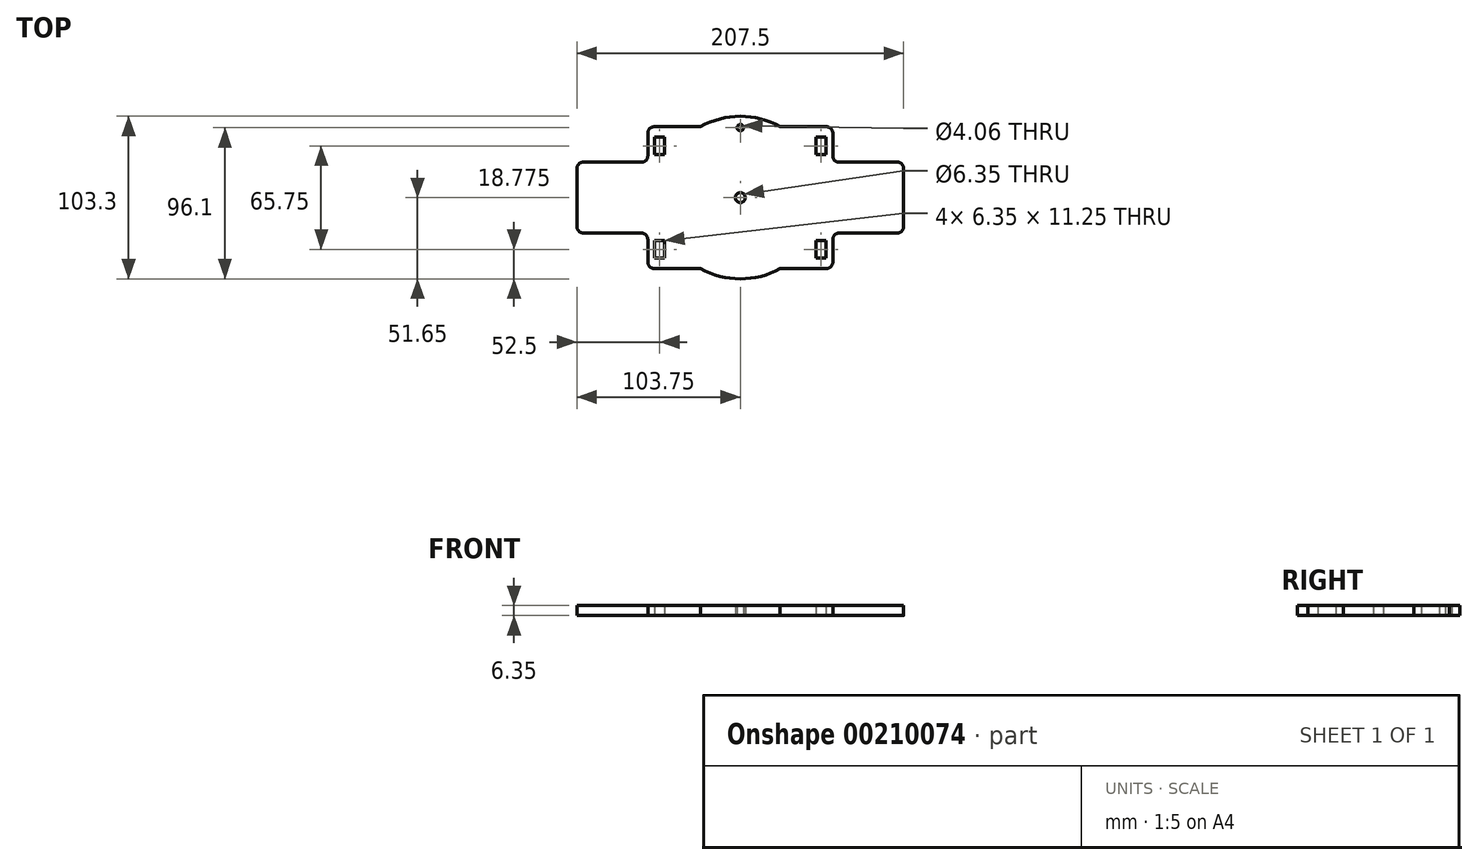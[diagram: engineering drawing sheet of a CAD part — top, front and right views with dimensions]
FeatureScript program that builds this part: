
annotation { "Feature Type Name" : "Feature", "Feature Type Description" : "" }
export const myFeature = defineFeature(function(context is Context, id is Id, definition is map)
    precondition{}
    {
        {
            var Q0;
            Q0=qCreatedBy(makeId("Top.planeOp"),FACE);
            var sketch = newSketch(context, id + "F0", { "sketchPlane" : qUnion([Q0])});
            skCircle(sketch, "E0", {"center": v(0, 0) * mm, "radius": 51.65 * mm});
            skLineSegment(sketch, "E1.bottom", {"start": v(-54.75, 45) * mm, "end": v(103.75, 45) * mm});
            skLineSegment(sketch, "E1.top", {"start": v(-103.75, -45) * mm, "end": v(103.75, -45) * mm});
            skLineSegment(sketch, "E1.left", {"start": v(-103.75, 18.5) * mm, "end": v(-103.75, -45) * mm});
            skLineSegment(sketch, "E1.right", {"start": v(103.75, 45) * mm, "end": v(103.75, -45) * mm});
            skLineSegment(sketch, "E2", {"start": v(-103.75, 0) * mm, "end": v(103.75, 0) * mm, "construction": true});
            skLineSegment(sketch, "E3", {"start": v(0, 51.65) * mm, "end": v(0, -51.65) * mm, "construction": true});
            skPoint(sketch, "E3.endSnap0", {"position": v(0, -45) * mm});
            skLineSegment(sketch, "E4.bottom", {"start": v(-54.43, 38.5) * mm, "end": v(-48.08, 38.5) * mm});
            skLineSegment(sketch, "E4.top", {"start": v(-54.43, 27.25) * mm, "end": v(-48.08, 27.25) * mm});
            skLineSegment(sketch, "E4.left", {"start": v(-54.43, 38.5) * mm, "end": v(-54.43, 27.25) * mm});
            skLineSegment(sketch, "E4.right", {"start": v(-48.08, 38.5) * mm, "end": v(-48.08, 27.25) * mm});
            skPoint(sketch, "E4.middle", {"position": v(-51.25, 32.88) * mm});
            skLineSegment(sketch, "E5.bottom", {"start": v(-54.43, -27.25) * mm, "end": v(-48.08, -27.25) * mm});
            skLineSegment(sketch, "E5.top", {"start": v(-54.43, -38.5) * mm, "end": v(-48.08, -38.5) * mm});
            skLineSegment(sketch, "E5.left", {"start": v(-54.43, -27.25) * mm, "end": v(-54.43, -38.5) * mm});
            skLineSegment(sketch, "E5.right", {"start": v(-48.08, -27.25) * mm, "end": v(-48.08, -38.5) * mm});
            skPoint(sketch, "E5.middle", {"position": v(-51.25, -32.88) * mm});
            skLineSegment(sketch, "E6.bottom", {"start": v(54.43, -27.25) * mm, "end": v(48.08, -27.25) * mm});
            skLineSegment(sketch, "E6.top", {"start": v(54.43, -38.5) * mm, "end": v(48.08, -38.5) * mm});
            skLineSegment(sketch, "E6.left", {"start": v(54.43, -27.25) * mm, "end": v(54.43, -38.5) * mm});
            skLineSegment(sketch, "E6.right", {"start": v(48.08, -27.25) * mm, "end": v(48.08, -38.5) * mm});
            skPoint(sketch, "E6.middle", {"position": v(51.25, -32.87) * mm});
            skLineSegment(sketch, "E7.bottom", {"start": v(48.08, 38.5) * mm, "end": v(54.43, 38.5) * mm});
            skLineSegment(sketch, "E7.top", {"start": v(48.08, 27.25) * mm, "end": v(54.43, 27.25) * mm});
            skLineSegment(sketch, "E7.left", {"start": v(48.08, 38.5) * mm, "end": v(48.08, 27.25) * mm});
            skLineSegment(sketch, "E7.right", {"start": v(54.43, 38.5) * mm, "end": v(54.43, 27.25) * mm});
            skPoint(sketch, "E7.middle", {"position": v(51.25, 32.88) * mm});
            skLineSegment(sketch, "E8", {"start": v(-99.75, 22.5) * mm, "end": v(-62.75, 22.5) * mm});
            skLineSegment(sketch, "E9", {"start": v(-58.75, 26.5) * mm, "end": v(-58.75, 41) * mm});
            skPoint(sketch, "E10.newPointA", {"position": v(-103.75, 22.5) * mm});
            skPoint(sketch, "E10.newPointB", {"position": v(-103.75, 45) * mm});
            skArc(sketch, "E10.filletArc", {"start": v(-99.75, 22.5) * mm, "mid": v(-102.58, 21.33) * mm, "end": v(-103.75, 18.5) * mm});
            skPoint(sketch, "E11.visualSharp", {"position": v(-58.75, 22.5) * mm});
            skArc(sketch, "E11.filletArc", {"start": v(-62.75, 22.5) * mm, "mid": v(-59.92, 23.67) * mm, "end": v(-58.75, 26.5) * mm});
            skPoint(sketch, "E12.newPointA", {"position": v(-58.75, 45) * mm});
            skArc(sketch, "E12.filletArc", {"start": v(-54.75, 45) * mm, "mid": v(-57.58, 43.83) * mm, "end": v(-58.75, 41) * mm});
            skArc(sketch, "E13.MirrorCS", {"start": v(-54.75, -45) * mm, "mid": v(-57.58, -43.83) * mm, "end": v(-58.75, -41) * mm});
            skLineSegment(sketch, "E14.MirrorCS", {"start": v(-99.75, -22.5) * mm, "end": v(-62.75, -22.5) * mm});
            skLineSegment(sketch, "E15.MirrorCS", {"start": v(-58.75, -26.5) * mm, "end": v(-58.75, -41) * mm});
            skArc(sketch, "E16.MirrorCS", {"start": v(-62.75, -22.5) * mm, "mid": v(-59.92, -23.67) * mm, "end": v(-58.75, -26.5) * mm});
            skArc(sketch, "E17.MirrorCS", {"start": v(-99.75, -22.5) * mm, "mid": v(-102.58, -21.33) * mm, "end": v(-103.75, -18.5) * mm});
            skArc(sketch, "E18.MirrorCS", {"start": v(54.75, -45) * mm, "mid": v(57.58, -43.83) * mm, "end": v(58.75, -41) * mm});
            skLineSegment(sketch, "E19.MirrorCS", {"start": v(58.75, -26.5) * mm, "end": v(58.75, -41) * mm});
            skArc(sketch, "E20.MirrorCS", {"start": v(62.75, -22.5) * mm, "mid": v(59.92, -23.67) * mm, "end": v(58.75, -26.5) * mm});
            skLineSegment(sketch, "E21.MirrorCS", {"start": v(99.75, -22.5) * mm, "end": v(62.75, -22.5) * mm});
            skArc(sketch, "E22.MirrorCS", {"start": v(99.75, -22.5) * mm, "mid": v(102.58, -21.33) * mm, "end": v(103.75, -18.5) * mm});
            skArc(sketch, "E23.MirrorCS", {"start": v(54.75, 45) * mm, "mid": v(57.58, 43.83) * mm, "end": v(58.75, 41) * mm});
            skLineSegment(sketch, "E24.MirrorCS", {"start": v(99.75, 22.5) * mm, "end": v(62.75, 22.5) * mm});
            skLineSegment(sketch, "E25.MirrorCS", {"start": v(58.75, 26.5) * mm, "end": v(58.75, 41) * mm});
            skArc(sketch, "E26.MirrorCS", {"start": v(62.75, 22.5) * mm, "mid": v(59.92, 23.67) * mm, "end": v(58.75, 26.5) * mm});
            skArc(sketch, "E27.MirrorCS", {"start": v(99.75, 22.5) * mm, "mid": v(102.58, 21.33) * mm, "end": v(103.75, 18.5) * mm});
            skCircle(sketch, "E28", {"center": v(0, 0) * mm, "radius": 3.17 * mm});
            skCircle(sketch, "E29", {"center": v(0, 44.45) * mm, "radius": 2.03 * mm});
            skSolve(sketch);
        }
        {
            var Q0;
            {var subQ0=sQuery(id+"F0.wireOp",EDGE,"E1.bottom");var subQ1=sQuery(id+"F0.wireOp",EDGE,"E0");var subQ2=makeQuery(id+"F0.imprint","INTERSECT",VERTEX,{"disambiguationData":[OD(0.0)],"derivedFrom":[subQ1,subQ0]});Q0=makeQuery(id+"F0.imprint","IMPRINT",FACE,{"disambiguationData":[TD([[makeQuery(id+"F0.imprint","IMPRINT",EDGE,{"disambiguationData":[TD([[subQ2,-1.0]])],"derivedFrom":subQ1}),1.0]])]});}
            var Q1;
            {var subQ0=sQuery(id+"F0.wireOp",EDGE,"E1.top");var subQ1=sQuery(id+"F0.wireOp",EDGE,"E0");var subQ2=makeQuery(id+"F0.imprint","INTERSECT",VERTEX,{"disambiguationData":[OD(0.0)],"derivedFrom":[subQ1,subQ0]});Q1=makeQuery(id+"F0.imprint","IMPRINT",FACE,{"disambiguationData":[TD([[makeQuery(id+"F0.imprint","IMPRINT",EDGE,{"disambiguationData":[TD([[subQ2,-1.0]])],"derivedFrom":subQ1}),1.0]])]});}
            var Q2;
            {var subQ0=sQuery(id+"F0.wireOp",EDGE,"E1.bottom");var subQ1=sQuery(id+"F0.wireOp",EDGE,"E0");var subQ2=makeQuery(id+"F0.imprint","INTERSECT",VERTEX,{"disambiguationData":[OD(0.0)],"derivedFrom":[subQ1,subQ0]});Q2=makeQuery(id+"F0.imprint","IMPRINT",FACE,{"disambiguationData":[TD([[makeQuery(id+"F0.imprint","IMPRINT",EDGE,{"disambiguationData":[TD([[subQ2,1.0]])],"derivedFrom":subQ1}),1.0]])]});}
            var Q3;
            Q3=makeQuery(id+"F0.imprint","IMPRINT",FACE,{"disambiguationData":[TD([[makeQuery(id+"F0.imprint","IMPRINT",EDGE,{"derivedFrom":sQuery(id+"F0.wireOp",EDGE,"E4.bottom")}),1.0]])]});
            var Q4;
            Q4=makeQuery(id+"F0.imprint","IMPRINT",FACE,{"disambiguationData":[TD([[makeQuery(id+"F0.imprint","IMPRINT",EDGE,{"derivedFrom":sQuery(id+"F0.wireOp",EDGE,"E6.bottom")}),-1.0]])]});
            extrude(context, id + "F1", {"entities" : qUnion([Q0, Q1, Q2, Q3, Q4]), "depth" : 6.35 * mm});
        }
    });
